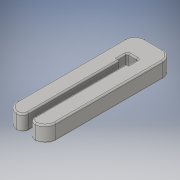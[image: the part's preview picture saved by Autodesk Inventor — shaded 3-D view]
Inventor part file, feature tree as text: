
AUTODESK INVENTOR PART (.ipt)
format: ipt  version: 2016 (Build 200138000, 138)  size: 187,392 bytes
history: native  units: in
note: dims shown in document units (in); Inventor stores cm internally (conversion verified against a paired STEP export)
features: fillet x4, extrude x1, sketch x1
ambient origin geometry x8: Origin, YZ Plane, XZ Plane, XY Plane, X Axis, Y Axis, Z Axis, Center Point
bodies: Solid1 (feature_tree)
feature tree (6):
  extrude  "Extrusion1"  Depth=0.125in
  fillet  "Fillet1"  Radius=0.068in
  fillet  "Fillet2"  Radius=0.017in
  fillet  "Fillet3"  Radius=0.017in
  fillet  "Fillet4"  Radius=1.5in
  sketch  "Sketch1"  dims[d15=0.1875in d16=0.0in d17=0.125in d18=0.068in d19=0.017in d28=0.017in d29=1.5in d30=0.45in d31=0.125in d32=0.125in d33=0.025in d34=0.025in d35=1.125in d36=1.125in d37=0.1875in d38=0.0687in]
